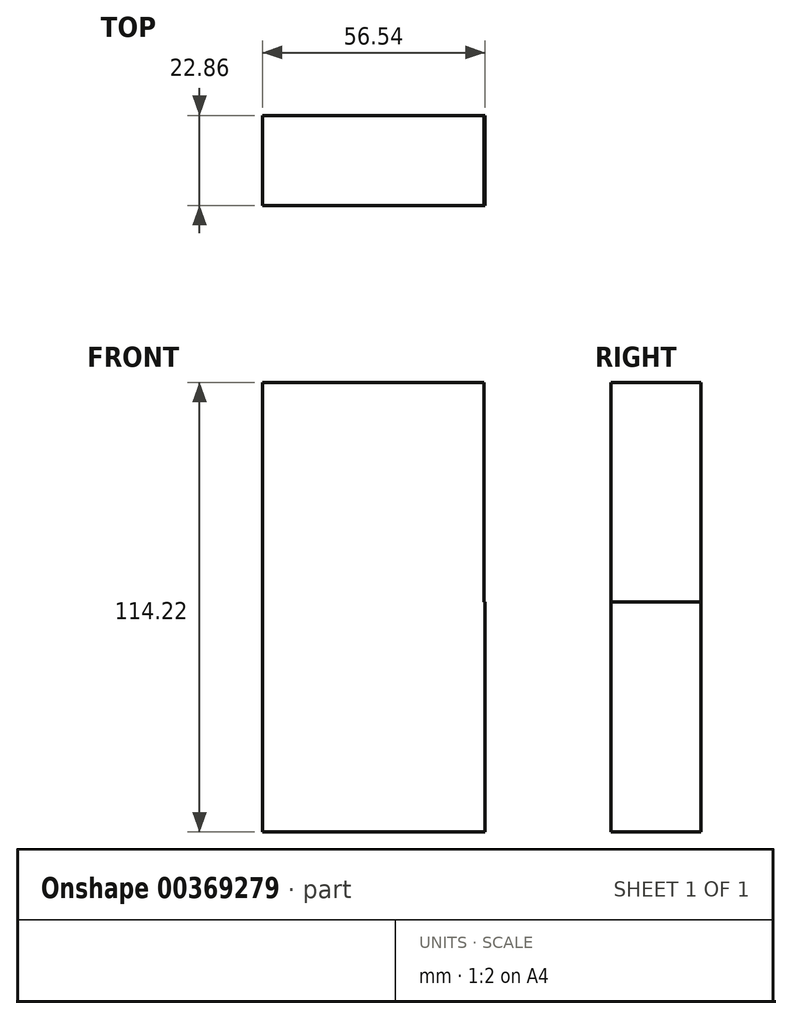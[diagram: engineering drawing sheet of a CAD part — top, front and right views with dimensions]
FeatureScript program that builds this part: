
annotation { "Feature Type Name" : "Feature", "Feature Type Description" : "" }
export const myFeature = defineFeature(function(context is Context, id is Id, definition is map)
    precondition{}
    {
        {
            var Q0;
            Q0=qCreatedBy(makeId("Front.planeOp"),FACE);
            var sketch = newSketch(context, id + "F0", { "sketchPlane" : qUnion([Q0])});
            skLineSegment(sketch, "E0.bottom", {"start": v(0, 0) * mm, "end": v(-28.27, 0) * mm});
            skLineSegment(sketch, "E0.top", {"start": v(0, -58.52) * mm, "end": v(-28.27, -58.52) * mm});
            skLineSegment(sketch, "E0.left", {"start": v(0, 0) * mm, "end": v(0, -58.52) * mm});
            skLineSegment(sketch, "E0.right", {"start": v(-28.27, 0) * mm, "end": v(-28.27, -58.52) * mm});
            skLineSegment(sketch, "E1.top", {"start": v(0, 55.7) * mm, "end": v(-28.27, 55.7) * mm});
            skLineSegment(sketch, "E1.left", {"start": v(0, 0) * mm, "end": v(0, 55.7) * mm});
            skLineSegment(sketch, "E1.right", {"start": v(-28.27, 0) * mm, "end": v(-28.27, 55.7) * mm});
            skLineSegment(sketch, "E2.bottom", {"start": v(0, 0) * mm, "end": v(27.99, 0) * mm});
            skLineSegment(sketch, "E2.top", {"start": v(0, 55.7) * mm, "end": v(27.99, 55.7) * mm});
            skLineSegment(sketch, "E2.right", {"start": v(27.99, 0) * mm, "end": v(27.99, 55.7) * mm});
            skLineSegment(sketch, "E3.bottom", {"start": v(0, 0) * mm, "end": v(28.27, 0) * mm});
            skLineSegment(sketch, "E3.top", {"start": v(0, -58.52) * mm, "end": v(28.27, -58.52) * mm});
            skLineSegment(sketch, "E3.right", {"start": v(28.27, 0) * mm, "end": v(28.27, -58.52) * mm});
            skSolve(sketch);
        }
        {
            var Q0;
            Q0 = qSketchRegion(id + "F0", true);
            extrude(context, id + "F1", {"entities" : qUnion([Q0]), "depth" : 22.86 * mm});
        }
    });
